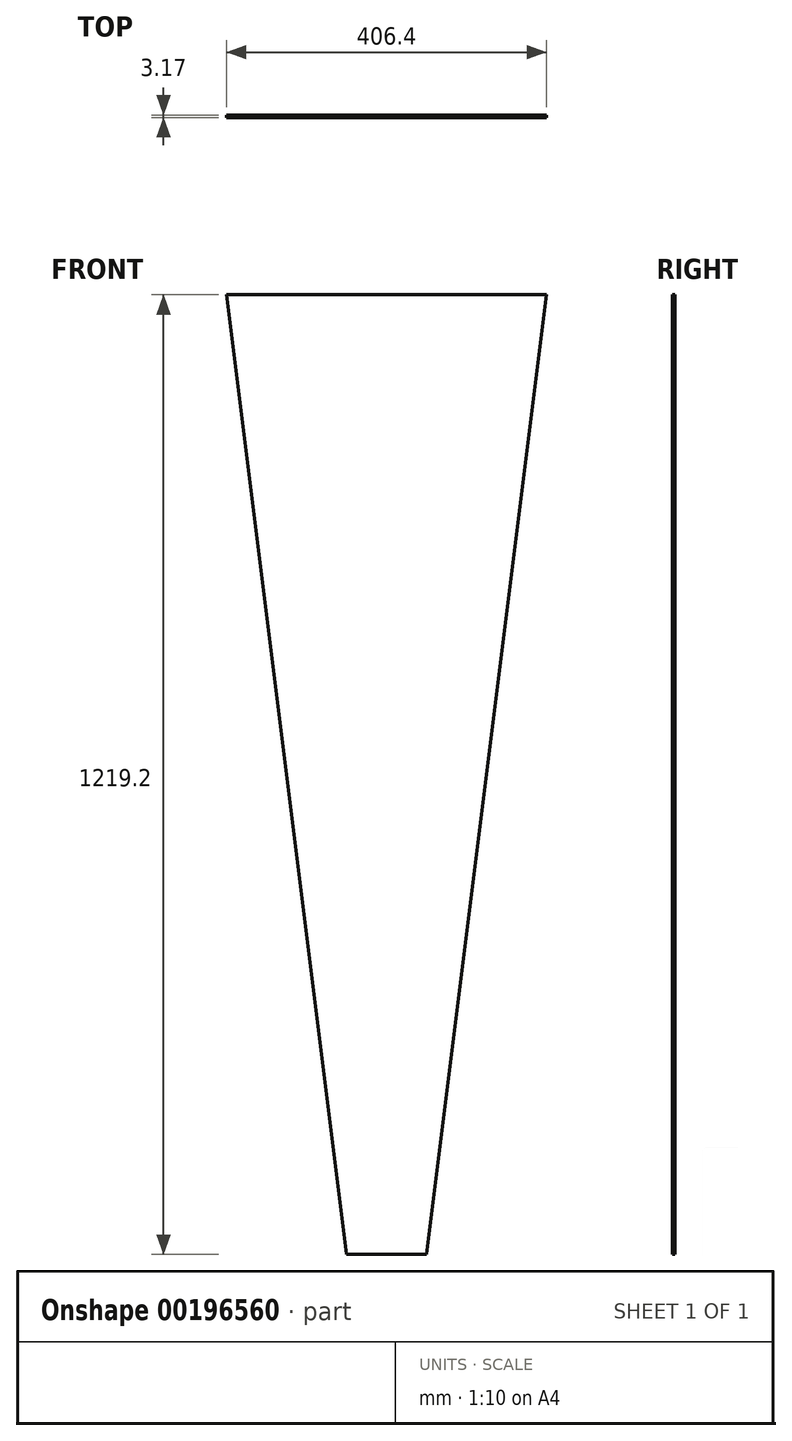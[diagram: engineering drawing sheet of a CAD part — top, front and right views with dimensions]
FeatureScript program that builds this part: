
annotation { "Feature Type Name" : "Feature", "Feature Type Description" : "" }
export const myFeature = defineFeature(function(context is Context, id is Id, definition is map)
    precondition{}
    {
        {
            var Q0;
            Q0=qCreatedBy(makeId("Front.planeOp"),FACE);
            var sketch = newSketch(context, id + "F0", { "sketchPlane" : qUnion([Q0])});
            skLineSegment(sketch, "E0.bottom", {"start": v(203.2, 762) * mm, "end": v(-203.2, 762) * mm});
            skLineSegment(sketch, "E0.top", {"start": v(50.8, -457.2) * mm, "end": v(-50.8, -457.2) * mm});
            skPoint(sketch, "E0.middle", {"position": v(0, 152.4) * mm});
            skLineSegment(sketch, "E1", {"start": v(-50.8, -457.2) * mm, "end": v(-203.2, 762) * mm});
            skLineSegment(sketch, "E2", {"start": v(50.8, -457.2) * mm, "end": v(203.2, 762) * mm});
            skPoint(sketch, "E3.orphan", {"position": v(-203.2, -457.2) * mm});
            skPoint(sketch, "E0.left.end.orphan", {"position": v(203.2, -457.2) * mm});
            skSolve(sketch);
        }
        {
            var Q0;
            Q0=makeQuery(id+"F0.imprint","IMPRINT",FACE,{"disambiguationData":[TD([[makeQuery(id+"F0.imprint","IMPRINT",EDGE,{"derivedFrom":sQuery(id+"F0.wireOp",EDGE,"E0.bottom")}),1.0]])]});
            extrude(context, id + "F1", {"entities" : qUnion([Q0]), "depth" : 3.17 * mm});
        }
    });
